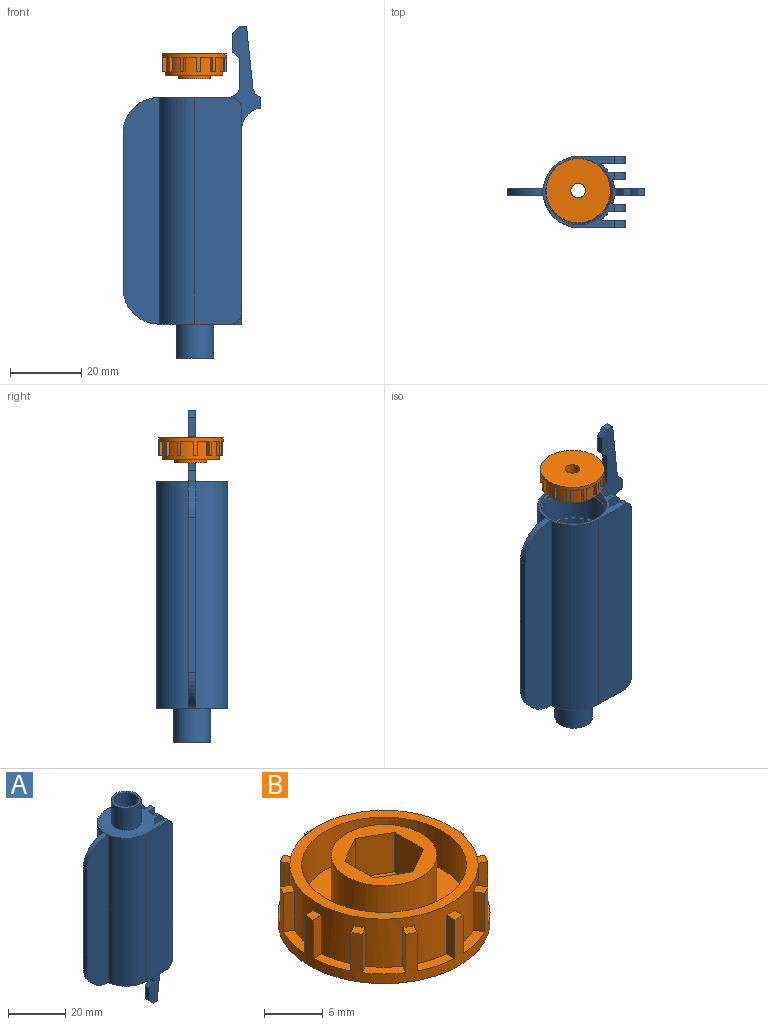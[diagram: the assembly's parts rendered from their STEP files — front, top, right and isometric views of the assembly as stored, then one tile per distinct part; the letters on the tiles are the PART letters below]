
ASSEMBLY  parts=2 mates=1
PART A: 152 faces, bbox 38.6x20.6x93 mm
  f0: plane 3x2mm, normal (1,0,0), area 6mm2, adj f1,f4,f149,f151
  f1: plane 83.5x8.55mm, normal (0,1,0), area 302.5mm2, adj f0,f2,f3,f6,f38,f144,f145,f146
  f2: plane 2x2mm, normal (0,0,-1), area 4mm2, adj f1,f4,f146,f147
  f3: plane 5.28x2mm, normal (-1,0,0), area 10.6mm2, adj f1,f4,f145,f146
  f4: plane 83.5x8.55mm, normal (0,-1,0), area 302.5mm2, adj f0,f2,f3,f9,f38,f144,f145,f146
  f5: plane 20.13x20mm, normal (0,0,-1), area 71.3mm2, adj f6,f7,f8,f9,f10,f39,f116,f119
  f6: cylinder r=10mm len=63.54mm, axis (0,0,1), area 163.5mm2, adj f1,f5,f38,f127,f148
  f7: cylinder r=10mm len=63.5mm, axis (0,0,1), area 933.8mm2, adj f5,f38,f119,f131
  f8: cylinder r=10mm len=63.5mm, axis (0,0,1), area 219mm2, adj f5,f38,f129,f130
  f9: cylinder r=10mm len=63.54mm, axis (0,0,1), area 163.5mm2, adj f4,f5,f38,f128,f148
  f10: cylinder r=10mm len=63.5mm, axis (0,0,1), area 219mm2, adj f5,f38,f125,f126
  f11: plane 1.34x1.14mm, normal (0,0,-1), area 1.2mm2, adj f40,f93,f97,f114
  f12: plane 1.51x1.39mm, normal (0,0,-1), area 1.2mm2, adj f40,f90,f94,f114
  f13: plane 1.58x1.53mm, normal (0,0,-1), area 1.2mm2, adj f40,f87,f91,f114
  f14: plane 1.58x1.53mm, normal (0,0,-1), area 1.2mm2, adj f40,f84,f88,f114
  f15: plane 1.51x1.39mm, normal (0,0,-1), area 1.2mm2, adj f40,f81,f85,f114
  f16: plane 1.34x1.14mm, normal (0,0,-1), area 1.2mm2, adj f40,f78,f82,f114
  f17: plane 1.34x1.14mm, normal (0,0,-1), area 1.2mm2, adj f40,f75,f79,f114
  f18: plane 1.51x1.39mm, normal (0,0,-1), area 1.2mm2, adj f40,f72,f76,f114
  f19: plane 1.58x1.53mm, normal (0,0,-1), area 1.2mm2, adj f40,f69,f73,f114
  f20: plane 1.58x1.53mm, normal (0,0,-1), area 1.2mm2, adj f40,f66,f70,f114
  f21: plane 1.51x1.39mm, normal (0,0,-1), area 1.2mm2, adj f40,f63,f67,f114
  f22: plane 1.34x1.14mm, normal (0,0,-1), area 1.2mm2, adj f40,f60,f64,f114
  f23: plane 1.34x1.14mm, normal (0,0,-1), area 1.2mm2, adj f40,f57,f61,f114
  f24: plane 1.51x1.39mm, normal (0,0,-1), area 1.2mm2, adj f40,f54,f58,f114
  f25: plane 1.58x1.53mm, normal (0,0,-1), area 1.2mm2, adj f40,f51,f55,f114
  f26: plane 1.58x1.53mm, normal (0,0,-1), area 1.2mm2, adj f40,f48,f52,f114
  f27: plane 1.51x1.39mm, normal (0,0,-1), area 1.2mm2, adj f40,f45,f49,f114
  f28: plane 1.34x1.14mm, normal (0,0,-1), area 1.2mm2, adj f40,f42,f46,f114
  f29: plane 1.34x1.14mm, normal (0,0,-1), area 1.2mm2, adj f40,f43,f111,f114
  f30: plane 1.51x1.39mm, normal (0,0,-1), area 1.2mm2, adj f40,f108,f112,f114
  f31: plane 1.58x1.53mm, normal (0,0,-1), area 1.2mm2, adj f40,f105,f109,f114
  f32: plane 1.58x1.53mm, normal (0,0,-1), area 1.2mm2, adj f40,f102,f106,f114
  f33: plane 1.51x1.39mm, normal (0,0,-1), area 1.2mm2, adj f40,f99,f103,f114
  f34: plane 1.34x1.14mm, normal (0,0,-1), area 1.2mm2, adj f40,f96,f100,f114
  f35: cylinder r=4.25mm len=11.5mm, axis (0,0,1), area 307.1mm2, adj f36,f41
  f36: plane 10.5x10.5mm, normal (0,0,1), area 29.8mm2, adj f35,f37
  f37: cylinder r=5.25mm len=10.5mm, axis (0,0,1), area 313.4mm2, adj f36,f38
  f38: plane 23.24x20mm, normal (0,0,1), area 262.1mm2, adj f1,f4,f6,f7,f8,f9,f10,f37
  f39: cylinder r=10mm len=63.5mm, axis (0,0,1), area 933.8mm2, adj f5,f38,f120,f124
  f40: cylinder r=8mm len=51mm, axis (0,0,1), area 2432.3mm2, adj f11,f12,f13,f14,f15,f16,f17,f18
  f41: plane 16x16mm, normal (0,0,-1), area 144.3mm2, adj f35,f40
  f42: plane 5x1mm, normal (1,0,0), area 5mm2, adj f28,f40,f44,f114
  f43: plane 5x1mm, normal (-1,0,0), area 5mm2, adj f29,f40,f44,f114
  f44: plane 1.02x1mm, normal (0,0,-1), area 1mm2, adj f40,f42,f43,f114
  f45: plane 5x0.97mm, normal (0.97,0.26,0), area 5mm2, adj f27,f40,f47,f114
  f46: plane 5x0.97mm, normal (-0.97,-0.26,0), area 5mm2, adj f28,f40,f47,f114
  f47: plane 1.23x1.23mm, normal (0,0,-1), area 1mm2, adj f40,f45,f46,f114
  f48: plane 5x0.87mm, normal (0.87,0.5,0), area 5mm2, adj f26,f40,f50,f114
  f49: plane 5x0.87mm, normal (-0.87,-0.5,0), area 5mm2, adj f27,f40,f50,f114
  f50: plane 1.37x1.37mm, normal (0,0,-1), area 1mm2, adj f40,f48,f49,f114
  f51: plane 5x0.71mm, normal (0.71,0.71,0), area 5mm2, adj f25,f40,f53,f114
  f52: plane 5x0.71mm, normal (-0.71,-0.71,0), area 5mm2, adj f26,f40,f53,f114
  f53: plane 1.42x1.42mm, normal (0,0,-1), area 1mm2, adj f40,f51,f52,f114
  f54: plane 5x0.87mm, normal (0.5,0.87,0), area 5mm2, adj f24,f40,f56,f114
  f55: plane 5x0.87mm, normal (-0.5,-0.87,0), area 5mm2, adj f25,f40,f56,f114
  f56: plane 1.37x1.37mm, normal (0,0,-1), area 1mm2, adj f40,f54,f55,f114
  f57: plane 5x0.97mm, normal (0.26,0.97,0), area 5mm2, adj f23,f40,f59,f114
  f58: plane 5x0.97mm, normal (-0.26,-0.97,0), area 5mm2, adj f24,f40,f59,f114
  f59: plane 1.23x1.23mm, normal (0,0,-1), area 1mm2, adj f40,f57,f58,f114
  f60: plane 5x1mm, normal (0,1,0), area 5mm2, adj f22,f40,f62,f114
  f61: plane 5x1mm, normal (0,-1,0), area 5mm2, adj f23,f40,f62,f114
  f62: plane 1.02x1mm, normal (0,0,-1), area 1mm2, adj f40,f60,f61,f114
  f63: plane 5x0.97mm, normal (-0.26,0.97,0), area 5mm2, adj f21,f40,f65,f114
  f64: plane 5x0.97mm, normal (0.26,-0.97,0), area 5mm2, adj f22,f40,f65,f114
  f65: plane 1.23x1.23mm, normal (0,0,-1), area 1mm2, adj f40,f63,f64,f114
  f66: plane 5x0.87mm, normal (-0.5,0.87,0), area 5mm2, adj f20,f40,f68,f114
  f67: plane 5x0.87mm, normal (0.5,-0.87,0), area 5mm2, adj f21,f40,f68,f114
  f68: plane 1.37x1.37mm, normal (0,0,-1), area 1mm2, adj f40,f66,f67,f114
  f69: plane 5x0.71mm, normal (-0.71,0.71,0), area 5mm2, adj f19,f40,f71,f114
  f70: plane 5x0.71mm, normal (0.71,-0.71,0), area 5mm2, adj f20,f40,f71,f114
  f71: plane 1.42x1.42mm, normal (0,0,-1), area 1mm2, adj f40,f69,f70,f114
  f72: plane 5x0.87mm, normal (-0.87,0.5,0), area 5mm2, adj f18,f40,f74,f114
  f73: plane 5x0.87mm, normal (0.87,-0.5,0), area 5mm2, adj f19,f40,f74,f114
  f74: plane 1.37x1.37mm, normal (0,0,-1), area 1mm2, adj f40,f72,f73,f114
  f75: plane 5x0.97mm, normal (-0.97,0.26,0), area 5mm2, adj f17,f40,f77,f114
  f76: plane 5x0.97mm, normal (0.97,-0.26,0), area 5mm2, adj f18,f40,f77,f114
  f77: plane 1.23x1.23mm, normal (0,0,-1), area 1mm2, adj f40,f75,f76,f114
  f78: plane 5x1mm, normal (-1,0,0), area 5mm2, adj f16,f40,f80,f114
  f79: plane 5x1mm, normal (1,0,0), area 5mm2, adj f17,f40,f80,f114
  f80: plane 1.02x1mm, normal (0,0,-1), area 1mm2, adj f40,f78,f79,f114
  f81: plane 5x0.97mm, normal (-0.97,-0.26,0), area 5mm2, adj f15,f40,f83,f114
  f82: plane 5x0.97mm, normal (0.97,0.26,0), area 5mm2, adj f16,f40,f83,f114
  f83: plane 1.23x1.23mm, normal (0,0,-1), area 1mm2, adj f40,f81,f82,f114
  f84: plane 5x0.87mm, normal (-0.87,-0.5,0), area 5mm2, adj f14,f40,f86,f114
  f85: plane 5x0.87mm, normal (0.87,0.5,0), area 5mm2, adj f15,f40,f86,f114
  f86: plane 1.37x1.37mm, normal (0,0,-1), area 1mm2, adj f40,f84,f85,f114
  f87: plane 5x0.71mm, normal (-0.71,-0.71,0), area 5mm2, adj f13,f40,f89,f114
  f88: plane 5x0.71mm, normal (0.71,0.71,0), area 5mm2, adj f14,f40,f89,f114
  f89: plane 1.42x1.42mm, normal (0,0,-1), area 1mm2, adj f40,f87,f88,f114
  f90: plane 5x0.87mm, normal (-0.5,-0.87,0), area 5mm2, adj f12,f40,f92,f114
  f91: plane 5x0.87mm, normal (0.5,0.87,0), area 5mm2, adj f13,f40,f92,f114
  f92: plane 1.37x1.37mm, normal (0,0,-1), area 1mm2, adj f40,f90,f91,f114
  f93: plane 5x0.97mm, normal (-0.26,-0.97,0), area 5mm2, adj f11,f40,f95,f114
  f94: plane 5x0.97mm, normal (0.26,0.97,0), area 5mm2, adj f12,f40,f95,f114
  f95: plane 1.23x1.23mm, normal (0,0,-1), area 1mm2, adj f40,f93,f94,f114
  f96: plane 5x1mm, normal (0,-1,0), area 5mm2, adj f34,f40,f98,f114
  f97: plane 5x1mm, normal (0,1,0), area 5mm2, adj f11,f40,f98,f114
  f98: plane 1.02x1mm, normal (0,0,-1), area 1mm2, adj f40,f96,f97,f114
  f99: plane 5x0.97mm, normal (0.26,-0.97,0), area 5mm2, adj f33,f40,f101,f114
  f100: plane 5x0.97mm, normal (-0.26,0.97,0), area 5mm2, adj f34,f40,f101,f114
  f101: plane 1.23x1.23mm, normal (0,0,-1), area 1mm2, adj f40,f99,f100,f114
  f102: plane 5x0.87mm, normal (0.5,-0.87,0), area 5mm2, adj f32,f40,f104,f114
  f103: plane 5x0.87mm, normal (-0.5,0.87,0), area 5mm2, adj f33,f40,f104,f114
  f104: plane 1.37x1.37mm, normal (0,0,-1), area 1mm2, adj f40,f102,f103,f114
  f105: plane 5x0.71mm, normal (0.71,-0.71,0), area 5mm2, adj f31,f40,f107,f114
  f106: plane 5x0.71mm, normal (-0.71,0.71,0), area 5mm2, adj f32,f40,f107,f114
  f107: plane 1.42x1.42mm, normal (0,0,-1), area 1mm2, adj f40,f105,f106,f114
  f108: plane 5x0.87mm, normal (0.87,-0.5,0), area 5mm2, adj f30,f40,f110,f114
  f109: plane 5x0.87mm, normal (-0.87,0.5,0), area 5mm2, adj f31,f40,f110,f114
  f110: plane 1.37x1.37mm, normal (0,0,-1), area 1mm2, adj f40,f108,f109,f114
  f111: plane 5x0.97mm, normal (0.97,-0.26,0), area 5mm2, adj f29,f40,f113,f114
  f112: plane 5x0.97mm, normal (-0.97,0.26,0), area 5mm2, adj f30,f40,f113,f114
  f113: plane 1.23x1.23mm, normal (0,0,-1), area 1mm2, adj f40,f111,f112,f114
  f114: cylinder r=9mm len=18mm, axis (0,0,1), area 615mm2, adj f11,f12,f13,f14,f15,f16,f17,f18
  f115: cylinder r=9.25mm len=18.5mm, axis (0,0,1), area 40.9mm2, adj f117,f118
  f116: cylinder r=9.25mm len=18.5mm, axis (0,0,1), area 29.1mm2, adj f5,f117
  f117: torus R=9.52mm, axis (0,0,1), area 69.7mm2, adj f115,f116
  f118: torus R=8.95mm, axis (0,0,1), area 24.2mm2, adj f114,f115
  f119: plane 63.5x10.18mm, normal (0,-1,0), area 603.2mm2, adj f5,f7,f38,f121,f122,f123
  f120: plane 63.5x10.18mm, normal (0,1,0), area 603.2mm2, adj f5,f38,f39,f121,f122,f123
  f121: plane 43.5x2mm, normal (-1,0,0), area 87mm2, adj f119,f120,f122,f123
  f122: cylinder r=10mm len=10mm, axis (0,1,0), area 31.4mm2, adj f38,f119,f120,f121
  f123: cylinder r=10mm len=10mm, axis (0,-1,0), area 31.4mm2, adj f5,f119,f120,f121
  f124: plane 63.5x13mm, normal (0,1,0), area 821.6mm2, adj f5,f38,f39,f132,f142,f143
  f125: plane 63.5x7mm, normal (0,-1,0), area 440.6mm2, adj f5,f10,f38,f132,f142,f143
  f126: plane 63.5x4.65mm, normal (0,1,0), area 291.3mm2, adj f5,f10,f38,f133,f140,f141
  f127: plane 63.5x3.63mm, normal (0,-1,0), area 226.8mm2, adj f5,f6,f38,f133,f140,f141
  f128: plane 63.5x3.63mm, normal (0,1,0), area 226.8mm2, adj f5,f9,f38,f134,f138,f139
  f129: plane 63.5x4.65mm, normal (0,-1,0), area 291.3mm2, adj f5,f8,f38,f134,f138,f139
  f130: plane 63.5x7mm, normal (0,1,0), area 440.6mm2, adj f5,f8,f38,f135,f136,f137
  f131: plane 63.5x13mm, normal (0,-1,0), area 821.6mm2, adj f5,f7,f38,f135,f136,f137
  f132: plane 57.5x2mm, normal (1,0,0), area 115mm2, adj f124,f125,f142,f143
  f133: plane 57.5x2mm, normal (1,0,0), area 115mm2, adj f126,f127,f140,f141
  f134: plane 57.5x2mm, normal (1,0,0), area 115mm2, adj f128,f129,f138,f139
  f135: plane 57.5x2mm, normal (1,0,0), area 115mm2, adj f130,f131,f136,f137
  f136: cylinder r=3mm len=3mm, axis (0,1,0), area 9.4mm2, adj f38,f130,f131,f135
  f137: cylinder r=3mm len=3mm, axis (0,-1,0), area 9.4mm2, adj f5,f130,f131,f135
  f138: cylinder r=3mm len=3mm, axis (0,1,0), area 9.4mm2, adj f38,f128,f129,f134
  f139: cylinder r=3mm len=3mm, axis (0,-1,0), area 9.4mm2, adj f5,f128,f129,f134
  f140: cylinder r=3mm len=3mm, axis (0,1,0), area 9.4mm2, adj f38,f126,f127,f133
  f141: cylinder r=3mm len=3mm, axis (0,-1,0), area 9.4mm2, adj f5,f126,f127,f133
  f142: cylinder r=3mm len=3mm, axis (0,1,0), area 9.4mm2, adj f38,f124,f125,f132
  f143: cylinder r=3mm len=3mm, axis (0,-1,0), area 9.4mm2, adj f5,f124,f125,f132
  f144: plane 8x2mm, normal (-1,0,0), area 16mm2, adj f1,f4,f145,f148
  f145: plane 2x1.98mm, normal (-0.65,0,0.76), area 5.2mm2, adj f1,f3,f4,f144
  f146: plane 2.02x2mm, normal (-0.71,0,-0.7), area 5.6mm2, adj f1,f2,f3,f4
  f147: plane 17.4x2mm, normal (0.99,0,-0.1), area 35mm2, adj f1,f2,f4,f149
  f148: cylinder r=3mm len=6.54mm, axis (0,-1,0), area 10.8mm2, adj f1,f4,f5,f6,f9,f144
  f149: cylinder r=3mm len=2.6mm, axis (0,-1,0), area 7.3mm2, adj f0,f1,f4,f147
  f150: plane 54.53x2mm, normal (1,0,0), area 109.1mm2, adj f1,f4,f38,f151
  f151: cylinder r=6mm len=5.97mm, axis (0,1,0), area 17.6mm2, adj f0,f1,f4,f150
PART B: 64 faces, bbox 18x18x7 mm
  f0: plane 9x9mm, normal (0,0,1), area 32.4mm2, adj f55,f56,f57,f58,f59,f60,f61
  f1: plane 3.56x1.82mm, normal (0,0,1), area 3.5mm2, adj f13,f40,f42,f51
  f2: plane 3.56x1.82mm, normal (0,0,1), area 3.5mm2, adj f13,f43,f45,f51
  f3: plane 3.11x3.11mm, normal (0,0,1), area 3.5mm2, adj f13,f46,f48,f51
  f4: plane 3.56x1.82mm, normal (0,0,1), area 3.5mm2, adj f13,f15,f49,f51
  f5: plane 3.56x1.82mm, normal (0,0,1), area 3.5mm2, adj f13,f16,f18,f51
  f6: plane 3.11x3.11mm, normal (0,0,1), area 3.5mm2, adj f13,f19,f21,f51
  f7: plane 3.56x1.82mm, normal (0,0,1), area 3.5mm2, adj f13,f22,f24,f51
  f8: plane 3.56x1.82mm, normal (0,0,1), area 3.5mm2, adj f13,f25,f27,f51
  f9: plane 3.11x3.11mm, normal (0,0,1), area 3.5mm2, adj f13,f28,f30,f51
  f10: plane 3.56x1.82mm, normal (0,0,1), area 3.5mm2, adj f13,f31,f33,f51
  f11: plane 3.56x1.82mm, normal (0,0,1), area 3.5mm2, adj f13,f34,f36,f51
  f12: plane 3.11x3.11mm, normal (0,0,1), area 3.5mm2, adj f13,f37,f39,f51
  f13: cylinder r=9mm len=18mm, axis (0,0,-1), area 104.6mm2, adj f1,f2,f3,f4,f5,f6,f7,f8
  f14: plane 18x18mm, normal (0,0,-1), area 241.3mm2, adj f13,f63
  f15: plane 4x1mm, normal (1,0,0), area 4mm2, adj f4,f13,f17,f51
  f16: plane 4x1mm, normal (-1,0,0), area 4mm2, adj f5,f13,f17,f51
  f17: plane 1.02x1mm, normal (0,0,1), area 1mm2, adj f13,f15,f16,f51
  f18: plane 4x0.87mm, normal (0.87,0.5,0), area 4mm2, adj f5,f13,f20,f51
  f19: plane 4x0.87mm, normal (-0.87,-0.5,0), area 4mm2, adj f6,f13,f20,f51
  f20: plane 1.37x1.37mm, normal (0,0,1), area 1mm2, adj f13,f18,f19,f51
  f21: plane 4x0.87mm, normal (0.5,0.87,0), area 4mm2, adj f6,f13,f23,f51
  f22: plane 4x0.87mm, normal (-0.5,-0.87,0), area 4mm2, adj f7,f13,f23,f51
  f23: plane 1.37x1.37mm, normal (0,0,1), area 1mm2, adj f13,f21,f22,f51
  f24: plane 4x1mm, normal (0,1,0), area 4mm2, adj f7,f13,f26,f51
  f25: plane 4x1mm, normal (0,-1,0), area 4mm2, adj f8,f13,f26,f51
  f26: plane 1.02x1mm, normal (0,0,1), area 1mm2, adj f13,f24,f25,f51
  f27: plane 4x0.87mm, normal (-0.5,0.87,0), area 4mm2, adj f8,f13,f29,f51
  f28: plane 4x0.87mm, normal (0.5,-0.87,0), area 4mm2, adj f9,f13,f29,f51
  f29: plane 1.37x1.37mm, normal (0,0,1), area 1mm2, adj f13,f27,f28,f51
  f30: plane 4x0.87mm, normal (-0.87,0.5,0), area 4mm2, adj f9,f13,f32,f51
  f31: plane 4x0.87mm, normal (0.87,-0.5,0), area 4mm2, adj f10,f13,f32,f51
  f32: plane 1.37x1.37mm, normal (0,0,1), area 1mm2, adj f13,f30,f31,f51
  f33: plane 4x1mm, normal (-1,0,0), area 4mm2, adj f10,f13,f35,f51
  f34: plane 4x1mm, normal (1,0,0), area 4mm2, adj f11,f13,f35,f51
  f35: plane 1.02x1mm, normal (0,0,1), area 1mm2, adj f13,f33,f34,f51
  f36: plane 4x0.87mm, normal (-0.87,-0.5,0), area 4mm2, adj f11,f13,f38,f51
  f37: plane 4x0.87mm, normal (0.87,0.5,0), area 4mm2, adj f12,f13,f38,f51
  f38: plane 1.37x1.37mm, normal (0,0,1), area 1mm2, adj f13,f36,f37,f51
  f39: plane 4x0.87mm, normal (-0.5,-0.87,0), area 4mm2, adj f12,f13,f41,f51
  f40: plane 4x0.87mm, normal (0.5,0.87,0), area 4mm2, adj f1,f13,f41,f51
  f41: plane 1.37x1.37mm, normal (0,0,1), area 1mm2, adj f13,f39,f40,f51
  f42: plane 4x1mm, normal (0,-1,0), area 4mm2, adj f1,f13,f44,f51
  f43: plane 4x1mm, normal (0,1,0), area 4mm2, adj f2,f13,f44,f51
  f44: plane 1.02x1mm, normal (0,0,1), area 1mm2, adj f13,f42,f43,f51
  f45: plane 4x0.87mm, normal (0.5,-0.87,0), area 4mm2, adj f2,f13,f47,f51
  f46: plane 4x0.87mm, normal (-0.5,0.87,0), area 4mm2, adj f3,f13,f47,f51
  f47: plane 1.37x1.37mm, normal (0,0,1), area 1mm2, adj f13,f45,f46,f51
  f48: plane 4x0.87mm, normal (0.87,-0.5,0), area 4mm2, adj f3,f13,f50,f51
  f49: plane 4x0.87mm, normal (-0.87,0.5,0), area 4mm2, adj f4,f13,f50,f51
  f50: plane 1.37x1.37mm, normal (0,0,1), area 1mm2, adj f13,f48,f49,f51
  f51: cylinder r=8mm len=16mm, axis (0,0,-1), area 203.3mm2, adj f1,f2,f3,f4,f5,f6,f7,f8
  f52: plane 16x16mm, normal (0,0,1), area 47.1mm2, adj f51,f53
  f53: cylinder r=7mm len=14mm, axis (0,0,1), area 175.9mm2, adj f52,f54
  f54: plane 14x14mm, normal (0,0,1), area 90.3mm2, adj f53,f55
  f55: cylinder r=4.5mm len=9mm, axis (0,0,-1), area 141.4mm2, adj f0,f54
  f56: plane 4.1x3.01mm, normal (-0.5,0.87,0), area 14.2mm2, adj f0,f57,f61,f62
  f57: plane 4.1x3.46mm, normal (-1,0,0), area 14.2mm2, adj f0,f56,f58,f62
  f58: plane 4.1x3mm, normal (-0.5,-0.86,0), area 14.2mm2, adj f0,f57,f59,f62
  f59: plane 4.1x3.01mm, normal (0.5,-0.87,0), area 14.2mm2, adj f0,f58,f60,f62
  f60: plane 4.1x3.46mm, normal (1,0,0), area 14.2mm2, adj f0,f59,f61,f62
  f61: plane 4.1x3mm, normal (0.5,0.86,0), area 14.2mm2, adj f0,f56,f60,f62
  f62: plane 6.93x6.01mm, normal (0,0,1), area 18mm2, adj f56,f57,f58,f59,f60,f61,f63
  f63: cylinder r=2.05mm len=4.1mm, axis (0,0,1), area 37.4mm2, adj f14,f62
PLACE A rot(axis=(1,0,0),180deg) t=(-3.67,-4.84,66.38)mm
PLACE B rot(axis=(0.07,-1,0),180deg) t=(-3.88,-4.54,94.08)mm
MATE parallel B.f63 <-> A.f6  axis (0,0,1) through (-3.88,-4.54,94.08)mm
